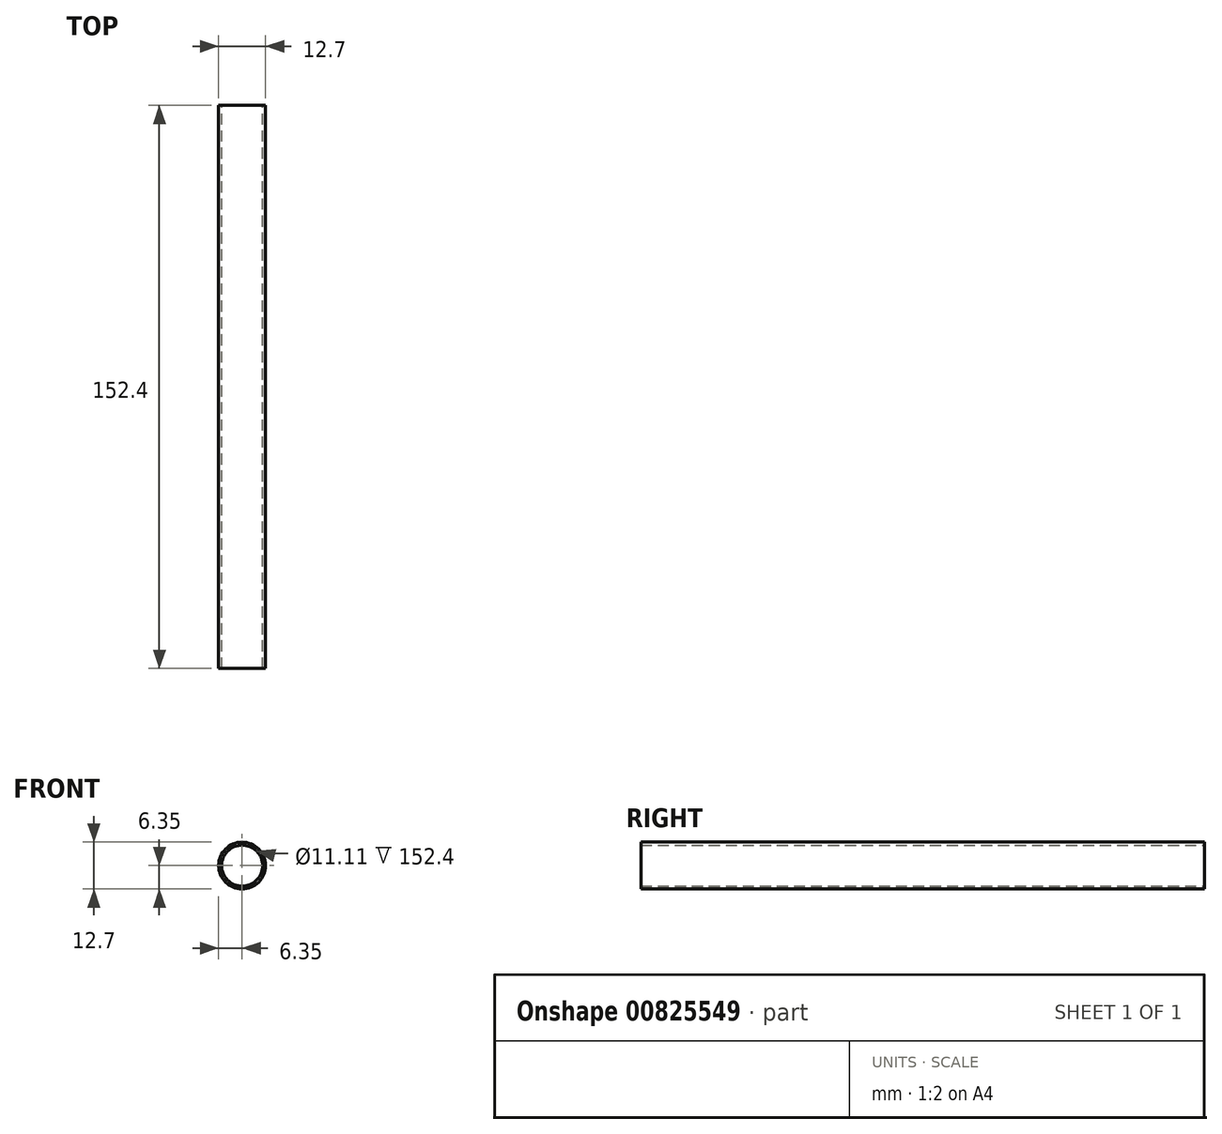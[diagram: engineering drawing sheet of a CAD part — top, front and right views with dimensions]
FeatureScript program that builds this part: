
annotation { "Feature Type Name" : "Feature", "Feature Type Description" : "" }
export const myFeature = defineFeature(function(context is Context, id is Id, definition is map)
    precondition{}
    {
        {
            var Q0;
            Q0=qCreatedBy(makeId("Front.planeOp"),FACE);
            var sketch = newSketch(context, id + "F0", { "sketchPlane" : qUnion([Q0])});
            skCircle(sketch, "E0", {"center": v(0, 0) * mm, "radius": 6.35 * mm});
            skCircle(sketch, "E1", {"center": v(0, 0) * mm, "radius": 5.56 * mm});
            skSolve(sketch);
        }
        {
            var Q0;
            Q0=makeQuery(id+"F0.imprint","IMPRINT",FACE,{"disambiguationData":[TD([[makeQuery(id+"F0.imprint","IMPRINT",EDGE,{"derivedFrom":sQuery(id+"F0.wireOp",EDGE,"E0")}),1.0]])]});
            extrude(context, id + "F1", {"entities" : qUnion([Q0]), "endBound" : BoundingType.SYMMETRIC, "depth" : 152.4 * mm, "offsetDistance" : 25.4 * mm});
        }
    });
